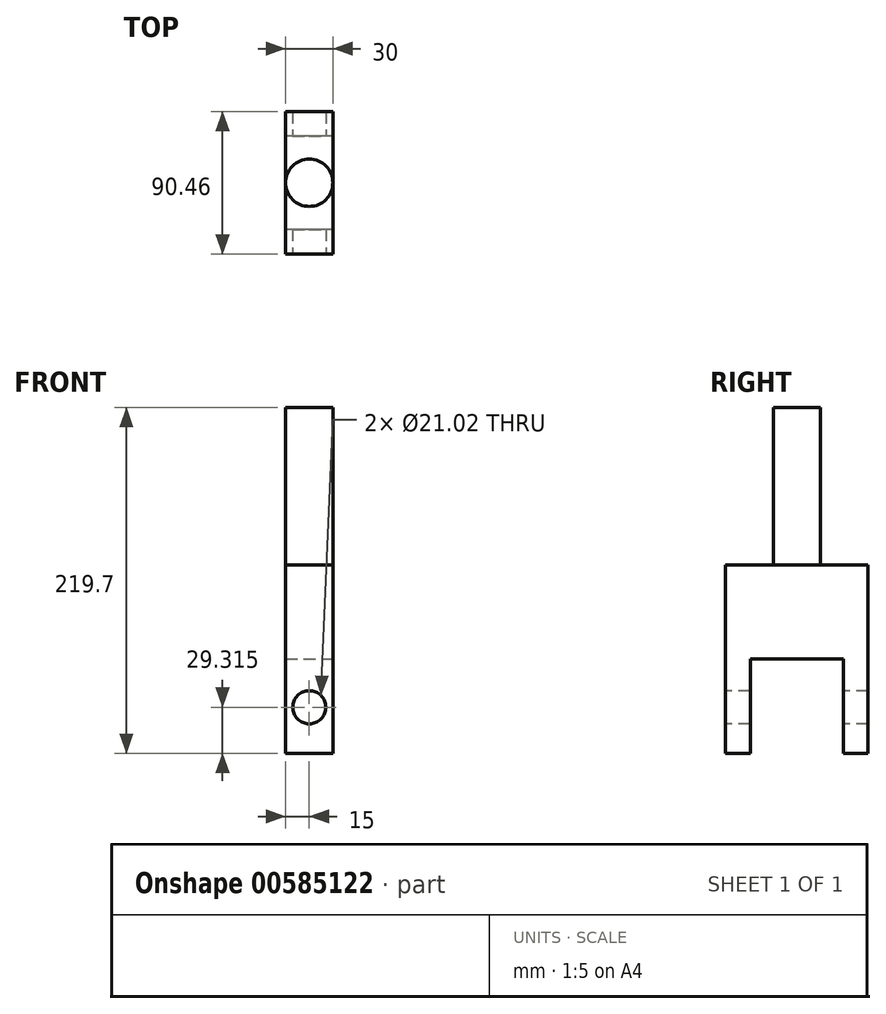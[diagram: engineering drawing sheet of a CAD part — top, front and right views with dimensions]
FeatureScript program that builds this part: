
annotation { "Feature Type Name" : "Feature", "Feature Type Description" : "" }
export const myFeature = defineFeature(function(context is Context, id is Id, definition is map)
    precondition{}
    {
        {
            var Q0;
            Q0=qCreatedBy(makeId("Right.planeOp"),FACE);
            var sketch = newSketch(context, id + "F0", { "sketchPlane" : qUnion([Q0])});
            skLineSegment(sketch, "E0.bottom", {"start": v(45.23, 59.85) * mm, "end": v(-45.23, 59.85) * mm});
            skLineSegment(sketch, "E0.top", {"start": v(45.23, -59.85) * mm, "end": v(-45.23, -59.85) * mm});
            skLineSegment(sketch, "E0.left", {"start": v(45.23, 59.85) * mm, "end": v(45.23, -59.85) * mm});
            skLineSegment(sketch, "E0.right", {"start": v(-45.23, 59.85) * mm, "end": v(-45.23, -59.85) * mm});
            skPoint(sketch, "E0.middle", {"position": v(0, 0) * mm});
            skSolve(sketch);
        }
        {
            var Q0;
            Q0 = qSketchRegion(id + "F0", true);
            extrude(context, id + "F1", {"entities" : qUnion([Q0]), "depth" : 30 * mm, "offsetDistance" : 25.4 * mm});
        }
        {
            var Q0;
            Q0=makeQuery(id+"F1.opExtrude","CAP_FACE",FACE,{"disambiguationData":[OSD([sQuery(id+"F0.wireOp",EDGE,"E0.bottom"),sQuery(id+"F0.wireOp",EDGE,"E0.top"),sQuery(id+"F0.wireOp",EDGE,"E0.left"),sQuery(id+"F0.wireOp",EDGE,"E0.right")])],"isStart":false});
            var sketch = newSketch(context, id + "F2", { "sketchPlane" : qUnion([Q0])});
            skLineSegment(sketch, "E1.bottom", {"start": v(29.62, 0) * mm, "end": v(-29.62, 0) * mm});
            skLineSegment(sketch, "E1.top", {"start": v(29.62, -119.7) * mm, "end": v(-29.62, -119.7) * mm});
            skLineSegment(sketch, "E1.left", {"start": v(29.62, 0) * mm, "end": v(29.62, -119.7) * mm});
            skLineSegment(sketch, "E1.right", {"start": v(-29.62, 0) * mm, "end": v(-29.62, -119.7) * mm});
            skPoint(sketch, "E1.middle", {"position": v(0, -59.85) * mm});
            skSolve(sketch);
        }
        {
            var Q0;
            Q0 = qSketchRegion(id + "F2", true);
            extrude(context, id + "F3", {"entities" : qUnion([Q0]), "operationType" : NewBodyOperationType.REMOVE, "oppositeDirection" : true, "depth" : 30 * mm, "offsetDistance" : 25.4 * mm});
        }
        {
            var Q0;
            Q0=makeQuery(id+"F1.opExtrude","SWEPT_FACE",FACE,{"disambiguationData":[OSD([sQuery(id+"F0.wireOp",EDGE,"E0.bottom")])]});
            var sketch = newSketch(context, id + "F4", { "sketchPlane" : qUnion([Q0])});
            skPoint(sketch, "E2", {"position": v(15, 0) * mm});
            skPoint(sketch, "E2.positionSnap0", {"position": v(15, 45.23) * mm});
            skPoint(sketch, "E2.positionSnap1", {"position": v(0, 0) * mm});
            skCircle(sketch, "E3", {"center": v(15, 0) * mm, "radius": 15 * mm});
            skSolve(sketch);
        }
        {
            var Q0;
            Q0 = qSketchRegion(id + "F4", true);
            extrude(context, id + "F5", {"entities" : qUnion([Q0]), "operationType" : NewBodyOperationType.ADD, "depth" : 100 * mm, "offsetDistance" : 25.4 * mm});
        }
        {
            var Q0;
            Q0=makeQuery(id+"F1.opExtrude","SWEPT_FACE",FACE,{"disambiguationData":[OSD([sQuery(id+"F0.wireOp",EDGE,"E0.right")])]});
            var sketch = newSketch(context, id + "F6", { "sketchPlane" : qUnion([Q0])});
            skPoint(sketch, "E4", {"position": v(15, -30.54) * mm});
            skPoint(sketch, "E4.positionSnap0", {"position": v(15, -59.85) * mm});
            skCircle(sketch, "E5", {"center": v(15, -30.54) * mm, "radius": 10.5 * mm});
            skSolve(sketch);
        }
        {
            var Q0;
            Q0=makeQuery(id+"F6.imprint","IMPRINT",FACE,{"disambiguationData":[TD([[makeQuery(id+"F6.imprint","IMPRINT",EDGE,{"derivedFrom":sQuery(id+"F6.wireOp",EDGE,"E5")}),1.0]])]});
            extrude(context, id + "F7", {"entities" : qUnion([Q0]), "operationType" : NewBodyOperationType.REMOVE, "oppositeDirection" : true, "depth" : 100 * mm, "offsetDistance" : 25.4 * mm});
        }
    });
